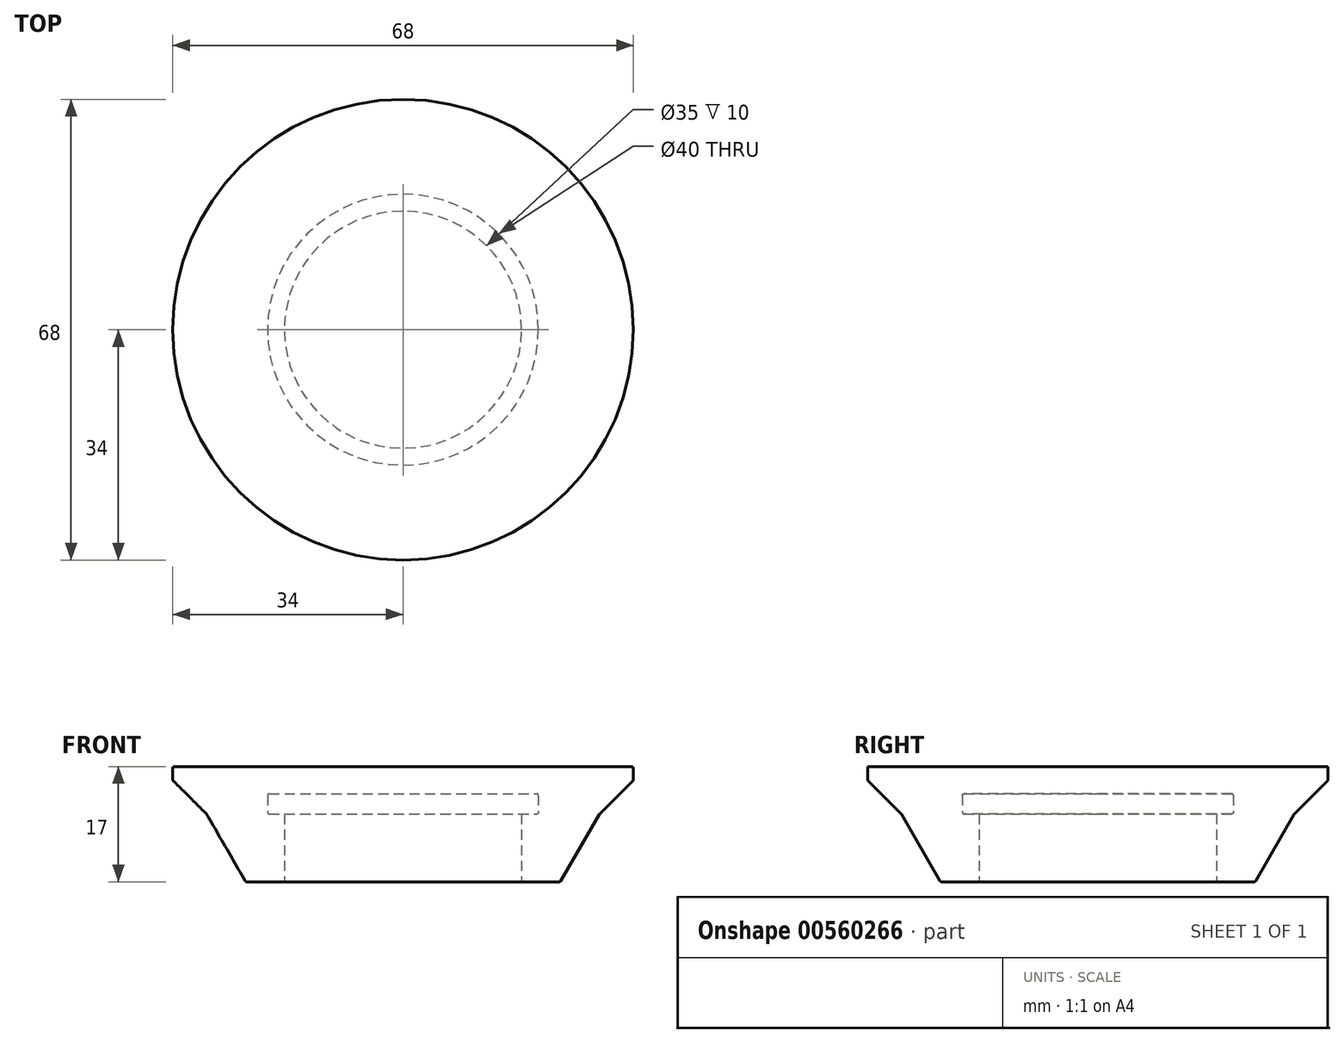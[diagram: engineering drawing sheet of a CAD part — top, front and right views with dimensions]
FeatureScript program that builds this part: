
annotation { "Feature Type Name" : "Feature", "Feature Type Description" : "" }
export const myFeature = defineFeature(function(context is Context, id is Id, definition is map)
    precondition{}
    {
        {
            var Q0;
            Q0=qCreatedBy(makeId("Top.planeOp"),FACE);
            var sketch = newSketch(context, id + "F0", { "sketchPlane" : qUnion([Q0])});
            skCircle(sketch, "E0", {"center": v(0, 0) * mm, "radius": 29 * mm});
            skSolve(sketch);
        }
        {
            var Q0;
            Q0=makeQuery(id+"F0.imprint","IMPRINT",FACE,{"disambiguationData":[TD([[makeQuery(id+"F0.imprint","IMPRINT",EDGE,{"derivedFrom":sQuery(id+"F0.wireOp",EDGE,"E0")}),1.0]])]});
            extrude(context, id + "F1", {"entities" : qUnion([Q0]), "depth" : 5 * mm, "offsetDistance" : 25 * mm, "hasDraft" : true, "draftAngle" : 45 * degree});
        }
        {
            var Q0;
            Q0=makeQuery(id+"F1.opExtrude","CAP_FACE",FACE,{"disambiguationData":[OSD([sQuery(id+"F0.wireOp",EDGE,"E0")])],"isStart":false});
            var sketch = newSketch(context, id + "F2", { "sketchPlane" : qUnion([Q0])});
            skCircle(sketch, "E1.0", {"center": v(0, 0) * mm, "radius": 34 * mm});
            skSolve(sketch);
        }
        {
            var Q0;
            Q0=makeQuery(id+"F2.imprint","IMPRINT",FACE,{"disambiguationData":[TD([[makeQuery(id+"F2.imprint","IMPRINT",EDGE,{"derivedFrom":sQuery(id+"F2.wireOp",EDGE,"E1.0")}),1.0]])]});
            extrude(context, id + "F3", {"entities" : qUnion([Q0]), "operationType" : NewBodyOperationType.ADD, "depth" : 2 * mm, "offsetDistance" : 25 * mm});
        }
        {
            var Q0;
            Q0=makeQuery(id+"F1.opExtrude","CAP_FACE",FACE,{"disambiguationData":[OSD([sQuery(id+"F0.wireOp",EDGE,"E0")])],"isStart":true});
            var sketch = newSketch(context, id + "F4", { "sketchPlane" : qUnion([Q0])});
            skSolve(sketch);
        }
        {
            var Q0;
            Q0 = qSketchRegion(id + "F4", true);
            var Q1;
            Q1=makeQuery(id+"F4.imprint","IMPRINT",FACE,{"disambiguationData":[TD([[makeQuery(id+"F4.imprint","IMPRINT",EDGE,{"derivedFrom":makeQuery(id+"F1.opExtrude","CAP_EDGE",EDGE,{"disambiguationData":[OSD([sQuery(id+"F0.wireOp",EDGE,"E0")])],"isStart":true})}),-1.0]])]});
            extrude(context, id + "F5", {"entities" : qUnion([Q0, Q1]), "operationType" : NewBodyOperationType.ADD, "depth" : 10 * mm, "offsetDistance" : 25 * mm, "hasDraft" : true, "draftAngle" : 30 * degree, "draftPullDirection" : true});
        }
        {
            var Q0;
            Q0=makeQuery(id+"F5.opExtrude","CAP_FACE",FACE,{"disambiguationData":[OSD([sQuery(id+"F0.wireOp",EDGE,"E0")])],"isStart":false});
            var sketch = newSketch(context, id + "F6", { "sketchPlane" : qUnion([Q0])});
            skCircle(sketch, "E2", {"center": v(0, 0) * mm, "radius": 17.5 * mm});
            skSolve(sketch);
        }
        {
            var Q0;
            Q0 = qSketchRegion(id + "F6", true);
            extrude(context, id + "F7", {"entities" : qUnion([Q0]), "operationType" : NewBodyOperationType.REMOVE, "oppositeDirection" : true, "depth" : 10 * mm, "offsetDistance" : 25 * mm});
        }
        {
            var Q0;
            Q0=qCreatedBy(makeId("Front.planeOp"),FACE);
            var sketch = newSketch(context, id + "F8", { "sketchPlane" : qUnion([Q0])});
            skLineSegment(sketch, "E3.bottom", {"start": v(0, 0) * mm, "end": v(20, 0) * mm});
            skLineSegment(sketch, "E3.top", {"start": v(0, 3) * mm, "end": v(20, 3) * mm});
            skLineSegment(sketch, "E3.left", {"start": v(0, 0) * mm, "end": v(0, 3) * mm});
            skLineSegment(sketch, "E3.right", {"start": v(20, 0) * mm, "end": v(20, 3) * mm});
            skLineSegment(sketch, "E4", {"start": v(0, 0) * mm, "end": v(0, -14.52) * mm});
            skSolve(sketch);
        }
        {
            var Q0;
            Q0 = qSketchRegion(id + "F8", true);
            var Q1;
            Q1=sQuery(id+"F8.wireOp",EDGE,"E4");
            revolve(context, id + "F9", {"operationType" : NewBodyOperationType.REMOVE, "entities" : qUnion([Q0]), "axis" : qUnion([Q1]), "revolveType" : RevolveType.FULL, "oppositeDirection" : true});
        }
        {
            var Q0;
            {var subQ0=sQuery(id+"F0.wireOp",EDGE,"E0");Q0=makeQuery(id+"F5.boolean.opBoolean","MERGE",EDGE,{"derivedFrom":[makeQuery(id+"F1.opExtrude","CAP_EDGE",EDGE,{"disambiguationData":[OSD([subQ0])],"isStart":true}),makeQuery(id+"F5.opExtrude","CAP_EDGE",EDGE,{"disambiguationData":[OSD([subQ0])],"isStart":true})]});}
            var Q1;
            Q1=makeQuery(id+"F3.opExtrude","CAP_EDGE",EDGE,{"disambiguationData":[OSD([sQuery(id+"F2.wireOp",EDGE,"E1.0")])],"isStart":false});
            var Q2;
            Q2=makeQuery(id+"F7.boolean.opBoolean","COPY",EDGE,{"derivedFrom":makeQuery(id+"F7.opExtrude","CAP_EDGE",EDGE,{"disambiguationData":[OSD([sQuery(id+"F6.wireOp",EDGE,"E2")])],"isStart":true})});
            var Q3;
            Q3=makeQuery(id+"F3.boolean.opBoolean","MERGE",EDGE,{"derivedFrom":[makeQuery(id+"F1.opExtrude","CAP_EDGE",EDGE,{"disambiguationData":[OSD([sQuery(id+"F0.wireOp",EDGE,"E0")])],"isStart":false}),makeQuery(id+"F3.opExtrude","CAP_EDGE",EDGE,{"disambiguationData":[OSD([sQuery(id+"F2.wireOp",EDGE,"E1.0")])],"isStart":true})]});
            var Q4;
            Q4=makeQuery(id+"F5.opExtrude","CAP_EDGE",EDGE,{"disambiguationData":[OSD([sQuery(id+"F0.wireOp",EDGE,"E0")])],"isStart":false});
            var Q5;
            Q5=makeQuery(id+"F9.boolean.opBoolean","COPY",EDGE,{"derivedFrom":makeQuery(id+"F9.opRevolve","SWEPT_EDGE",EDGE,{"disambiguationData":[OSD([sQuery(id+"F8.wireOp",EDGE,"E3.bottom"),sQuery(id+"F8.wireOp",EDGE,"E3.right")])]})});
            var Q6;
            Q6=makeQuery(id+"F7.boolean.opBoolean","COPY",EDGE,{"derivedFrom":makeQuery(id+"F7.opExtrude","CAP_EDGE",EDGE,{"disambiguationData":[OSD([sQuery(id+"F6.wireOp",EDGE,"E2")])],"isStart":false})});
            var Q7;
            Q7=makeQuery(id+"F9.boolean.opBoolean","COPY",EDGE,{"derivedFrom":makeQuery(id+"F9.opRevolve","SWEPT_EDGE",EDGE,{"disambiguationData":[OSD([sQuery(id+"F8.wireOp",EDGE,"E3.top"),sQuery(id+"F8.wireOp",EDGE,"E3.right")])]})});
            fillet(context, id + "F10", {"entities" : qUnion([Q0, Q1, Q2, Q3, Q4, Q5, Q6, Q7]), "radius" : .25 * mm, "tangentPropagation" : true, "allowEdgeOverflow" : false});
        }
    });
